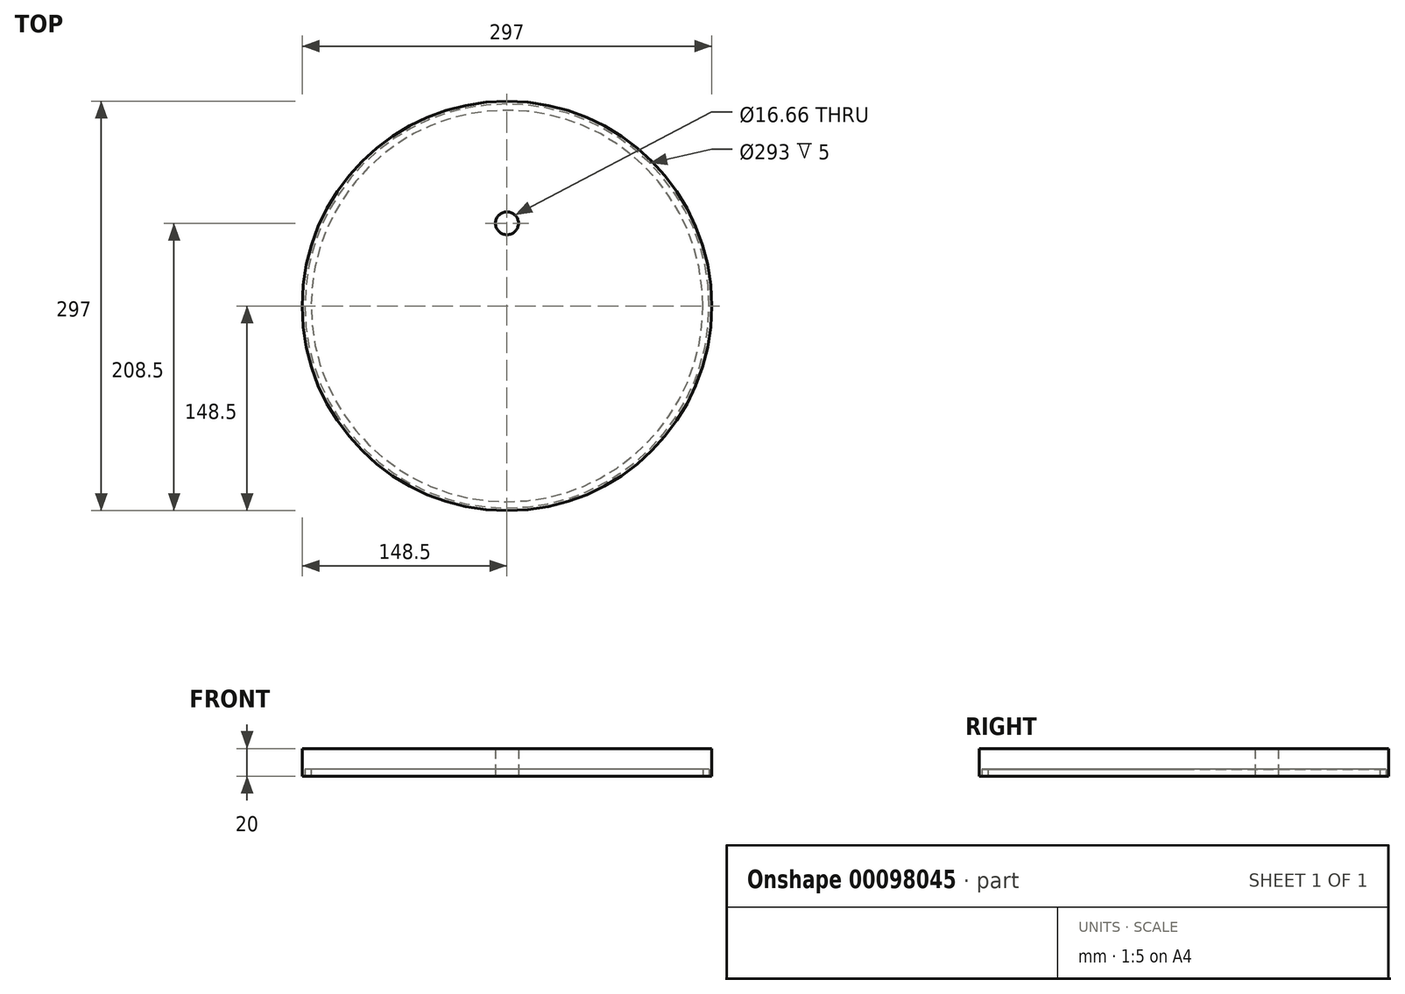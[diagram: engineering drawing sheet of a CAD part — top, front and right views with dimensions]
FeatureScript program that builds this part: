
annotation { "Feature Type Name" : "Feature", "Feature Type Description" : "" }
export const myFeature = defineFeature(function(context is Context, id is Id, definition is map)
    precondition{}
    {
        {
            var Q0;
            Q0=qCreatedBy(makeId("Top.planeOp"),FACE);
            var sketch = newSketch(context, id + "F0", { "sketchPlane" : qUnion([Q0])});
            skCircle(sketch, "E0", {"center": v(0, 0) * mm, "radius": 148.5 * mm});
            skLineSegment(sketch, "E1", {"start": v(-25, 103.3) * mm, "end": v(25, 103.3) * mm, "construction": true});
            skCircle(sketch, "E2", {"center": v(0, 60) * mm, "radius": 8.33 * mm});
            skLineSegment(sketch, "E3", {"start": v(-25, 103.3) * mm, "end": v(0, 60) * mm, "construction": true});
            skLineSegment(sketch, "E4", {"start": v(25, 103.3) * mm, "end": v(0, 60) * mm, "construction": true});
            skLineSegment(sketch, "E5", {"start": v(0, 60) * mm, "end": v(0, 0) * mm, "construction": true});
            skLineSegment(sketch, "E6", {"start": v(0, 60) * mm, "end": v(0, 103.3) * mm, "construction": true});
            skSolve(sketch);
        }
        {
            var Q0;
            Q0=makeQuery(id+"F0.imprint","IMPRINT",FACE,{"disambiguationData":[TD([[makeQuery(id+"F0.imprint","IMPRINT",EDGE,{"derivedFrom":sQuery(id+"F0.wireOp",EDGE,"E0")}),1.0]])]});
            var Q1;
            Q1=makeQuery(id+"F0.imprint","IMPRINT",FACE,{"disambiguationData":[TD([[makeQuery(id+"F0.imprint","IMPRINT",EDGE,{"derivedFrom":sQuery(id+"F0.wireOp",EDGE,"LIXrByum-44Gz-KbWN-PE50-DMeDG7NppI0J")}),1.0]])]});
            var Q2;
            Q2=makeQuery(id+"F0.imprint","IMPRINT",FACE,{"disambiguationData":[TD([[makeQuery(id+"F0.imprint","IMPRINT",EDGE,{"derivedFrom":sQuery(id+"F0.wireOp",EDGE,"oq2Y4278-V4UZ-WgQw-2GIa-DsGsglEtdsp5")}),1.0]])]});
            extrude(context, id + "F1", {"entities" : qUnion([Q0, Q1, Q2]), "depth" : 20 * mm});
        }
        {
            var Q0;
            Q0=makeQuery(id+"F0.imprint","IMPRINT",FACE,{"disambiguationData":[TD([[makeQuery(id+"F0.imprint","IMPRINT",EDGE,{"derivedFrom":sQuery(id+"F0.wireOp",EDGE,"E0")}),1.0]])]});
            var sketch = newSketch(context, id + "F2", { "sketchPlane" : qUnion([Q0])});
            skCircle(sketch, "E7", {"center": v(0, 0) * mm, "radius": 146.5 * mm});
            skCircle(sketch, "E8", {"center": v(0, 0) * mm, "radius": 142 * mm});
            skSolve(sketch);
        }
        {
            var Q0;
            Q0=qSketchRegion(id+"F2",true);
            extrude(context, id + "F3", {"entities" : qUnion([Q0]), "operationType" : NewBodyOperationType.REMOVE, "depth" : 5 * mm});
        }
    });
